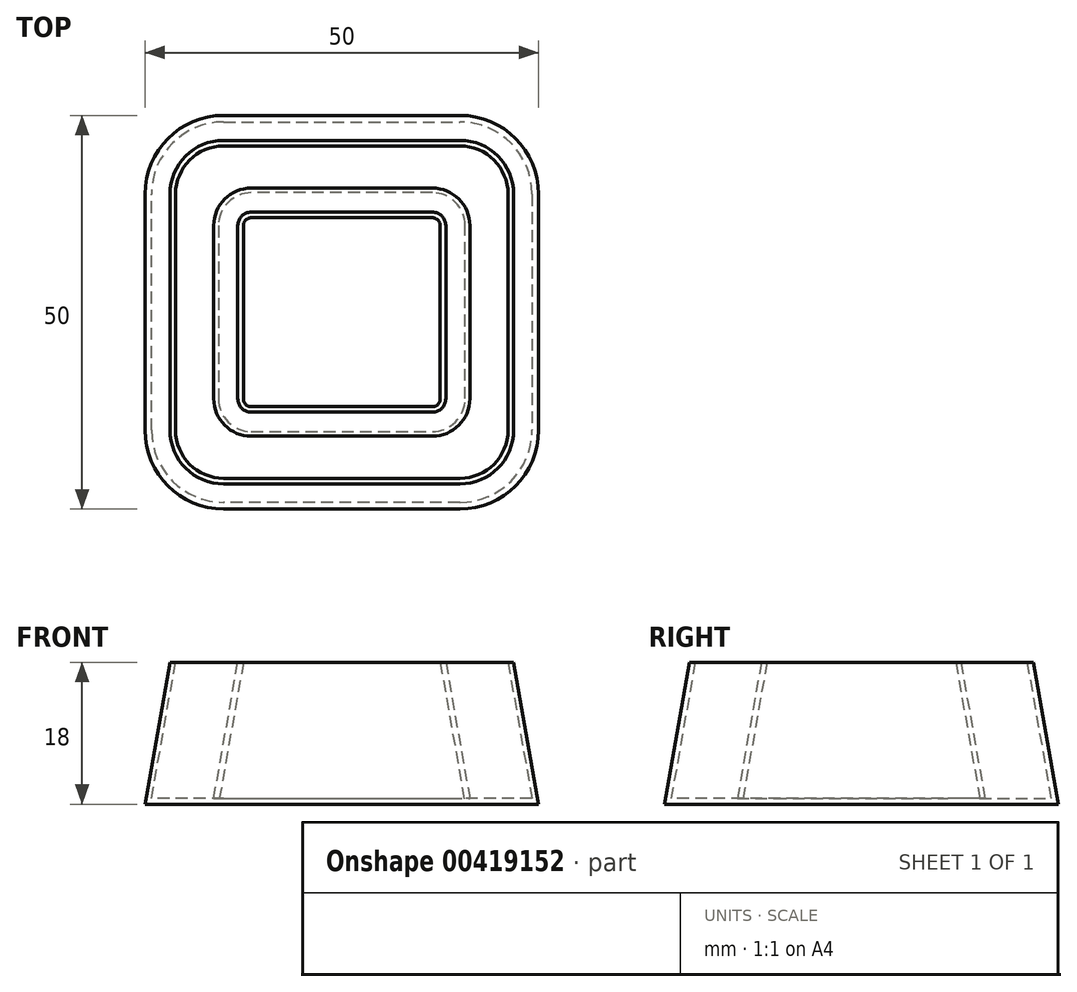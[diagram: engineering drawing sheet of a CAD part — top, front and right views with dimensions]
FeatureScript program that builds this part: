
annotation { "Feature Type Name" : "Feature", "Feature Type Description" : "" }
export const myFeature = defineFeature(function(context is Context, id is Id, definition is map)
    precondition{}
    {
        {
            var Q0;
            Q0=qCreatedBy(makeId("Top.planeOp"),FACE);
            var sketch = newSketch(context, id + "F0", { "sketchPlane" : qUnion([Q0])});
            skLineSegment(sketch, "E0.bottom", {"start": v(15, 25) * mm, "end": v(-15, 25) * mm});
            skLineSegment(sketch, "E0.top", {"start": v(15, -25) * mm, "end": v(-15, -25) * mm});
            skLineSegment(sketch, "E0.left", {"start": v(25, 15) * mm, "end": v(25, -15) * mm});
            skLineSegment(sketch, "E0.right", {"start": v(-25, 15) * mm, "end": v(-25, -15) * mm});
            skPoint(sketch, "E0.middle", {"position": v(0, 0) * mm});
            skPoint(sketch, "E1.visualSharp", {"position": v(-25, 25) * mm});
            skArc(sketch, "E1.filletArc", {"start": v(-15, 25) * mm, "mid": v(-22.07, 22.07) * mm, "end": v(-25, 15) * mm});
            skPoint(sketch, "E2.visualSharp", {"position": v(25, 25) * mm});
            skArc(sketch, "E2.filletArc", {"start": v(25, 15) * mm, "mid": v(22.07, 22.07) * mm, "end": v(15, 25) * mm});
            skPoint(sketch, "E3.visualSharp", {"position": v(25, -25) * mm});
            skArc(sketch, "E3.filletArc", {"start": v(15, -25) * mm, "mid": v(22.07, -22.07) * mm, "end": v(25, -15) * mm});
            skPoint(sketch, "E4.visualSharp", {"position": v(-25, -25) * mm});
            skArc(sketch, "E4.filletArc", {"start": v(-25, -15) * mm, "mid": v(-22.07, -22.07) * mm, "end": v(-15, -25) * mm});
            skSolve(sketch);
        }
        {
            var Q0;
            Q0=qSketchRegion(id+"F0",true);
            extrude(context, id + "F1", {"entities" : qUnion([Q0]), "depth" : 18 * mm, "hasDraft" : true, "draftAngle" : 10 * degree, "draftPullDirection" : true});
        }
        {
            var Q0;
            Q0=makeQuery(id+"F1.opExtrude","CAP_FACE",FACE,{"disambiguationData":[OSD([sQuery(id+"F0.wireOp",EDGE,"E0.bottom"),sQuery(id+"F0.wireOp",EDGE,"E0.top"),sQuery(id+"F0.wireOp",EDGE,"E0.left"),sQuery(id+"F0.wireOp",EDGE,"E0.right"),sQuery(id+"F0.wireOp",EDGE,"E1.filletArc"),sQuery(id+"F0.wireOp",EDGE,"E2.filletArc"),sQuery(id+"F0.wireOp",EDGE,"E3.filletArc"),sQuery(id+"F0.wireOp",EDGE,"E4.filletArc")])],"isStart":false});
            var sketch = newSketch(context, id + "F2", { "sketchPlane" : qUnion([Q0])});
            skLineSegment(sketch, "E5.bottom", {"start": v(11.5, 12) * mm, "end": v(-11.5, 12) * mm});
            skLineSegment(sketch, "E5.top", {"start": v(11.5, -12) * mm, "end": v(-11.5, -12) * mm});
            skLineSegment(sketch, "E5.left", {"start": v(12.5, 11) * mm, "end": v(12.5, -11) * mm});
            skLineSegment(sketch, "E5.right", {"start": v(-12.5, 11) * mm, "end": v(-12.5, -11) * mm});
            skPoint(sketch, "E5.middle", {"position": v(0, 0) * mm});
            skPoint(sketch, "E6.visualSharp", {"position": v(-12.5, 12) * mm});
            skArc(sketch, "E6.filletArc", {"start": v(-11.5, 12) * mm, "mid": v(-12.2, 11.7) * mm, "end": v(-12.5, 11) * mm});
            skPoint(sketch, "E7.visualSharp", {"position": v(12.5, 12) * mm});
            skArc(sketch, "E7.filletArc", {"start": v(12.5, 11) * mm, "mid": v(12.2, 11.7) * mm, "end": v(11.5, 12) * mm});
            skPoint(sketch, "E8.visualSharp", {"position": v(12.5, -12) * mm});
            skArc(sketch, "E8.filletArc", {"start": v(11.5, -12) * mm, "mid": v(12.2, -11.7) * mm, "end": v(12.5, -11) * mm});
            skPoint(sketch, "E9.visualSharp", {"position": v(-12.5, -12) * mm});
            skArc(sketch, "E9.filletArc", {"start": v(-12.5, -11) * mm, "mid": v(-12.2, -11.7) * mm, "end": v(-11.5, -12) * mm});
            skSolve(sketch);
        }
        {
            var Q0;
            Q0=makeQuery(id+"F2.imprint","IMPRINT",FACE,{"disambiguationData":[TD([[makeQuery(id+"F2.imprint","IMPRINT",EDGE,{"derivedFrom":sQuery(id+"F2.wireOp",EDGE,"E5.bottom")}),1.0]])]});
            extrude(context, id + "F3", {"entities" : qUnion([Q0]), "operationType" : NewBodyOperationType.REMOVE, "endBound" : BoundingType.THROUGH_ALL, "oppositeDirection" : true, "depth" : 25 * mm, "hasDraft" : true, "draftAngle" : 10 * degree});
        }
        {
            var Q0;
            Q0=makeQuery(id+"F1.opExtrude","CAP_FACE",FACE,{"disambiguationData":[OSD([sQuery(id+"F0.wireOp",EDGE,"E0.bottom"),sQuery(id+"F0.wireOp",EDGE,"E0.top"),sQuery(id+"F0.wireOp",EDGE,"E0.left"),sQuery(id+"F0.wireOp",EDGE,"E0.right"),sQuery(id+"F0.wireOp",EDGE,"E1.filletArc"),sQuery(id+"F0.wireOp",EDGE,"E2.filletArc"),sQuery(id+"F0.wireOp",EDGE,"E3.filletArc"),sQuery(id+"F0.wireOp",EDGE,"E4.filletArc")])],"isStart":false});
            shell(context, id + "F4", {"entities" : qUnion([Q0]), "thickness" : 0.7 * mm});
        }
    });
